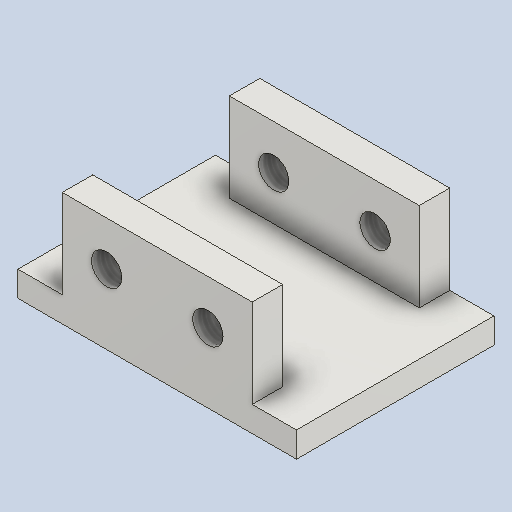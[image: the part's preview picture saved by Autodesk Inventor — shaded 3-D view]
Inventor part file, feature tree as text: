
AUTODESK INVENTOR PART (.ipt)
format: ipt  version: 2024 (Build 280153000, 153)  size: 501,248 bytes
history: native  units: mm
features: thread x4, extrude x3, sketch x3, mirror x1
ambient origin geometry x8: Origin, YZ Plane, XZ Plane, XY Plane, X Axis, Y Axis, Z Axis, Center Point
bodies: Solid1 (feature_tree)
feature tree (11):
  extrude  "Extrusion1"  Depth=110.0mm
  extrude  "Extrusion2"  Depth=39.0mm
  sketch  "Sketch3"  dims[d4=10.0mm d5=0.0mm d6=12.0mm d8=37.5mm d9=75.0mm d10=35.0mm d11=0.0mm d14=33.0mm d16=12.0mm d17=12.0mm d18=27.5mm d19=27.5mm d20=40.0mm d21=20.0mm d24=80.0mm d25=0.0mm d42=350.0mm d43=0.0mm d50=600.0mm d51=0.0mm d52=600.0mm d53=0.0mm d54=600.0mm d55=0.0mm d34=0.5mm d35=0.872665mm d36=0.5mm d37=0.872665mm]
  extrude  "Extrusion3"  Depth=12.0mm
  mirror  "Mirror1"
  thread  "Thread9"  [1 undecoded]
  thread  "Thread13"  [1 undecoded]
  thread  "Thread14"  [1 undecoded]
  thread  "Thread15"  [1 undecoded]
  sketch  "Sketch1"  dims[d0=78.0mm d1=110.0mm]
  sketch  "Sketch2"  dims[d2=55.0mm d3=39.0mm]
note: 4 required parameter values undecoded (feature->parameter linkage not recoverable at this tier; creation-order binding heuristic only, values carry confidence <= 0.55)
